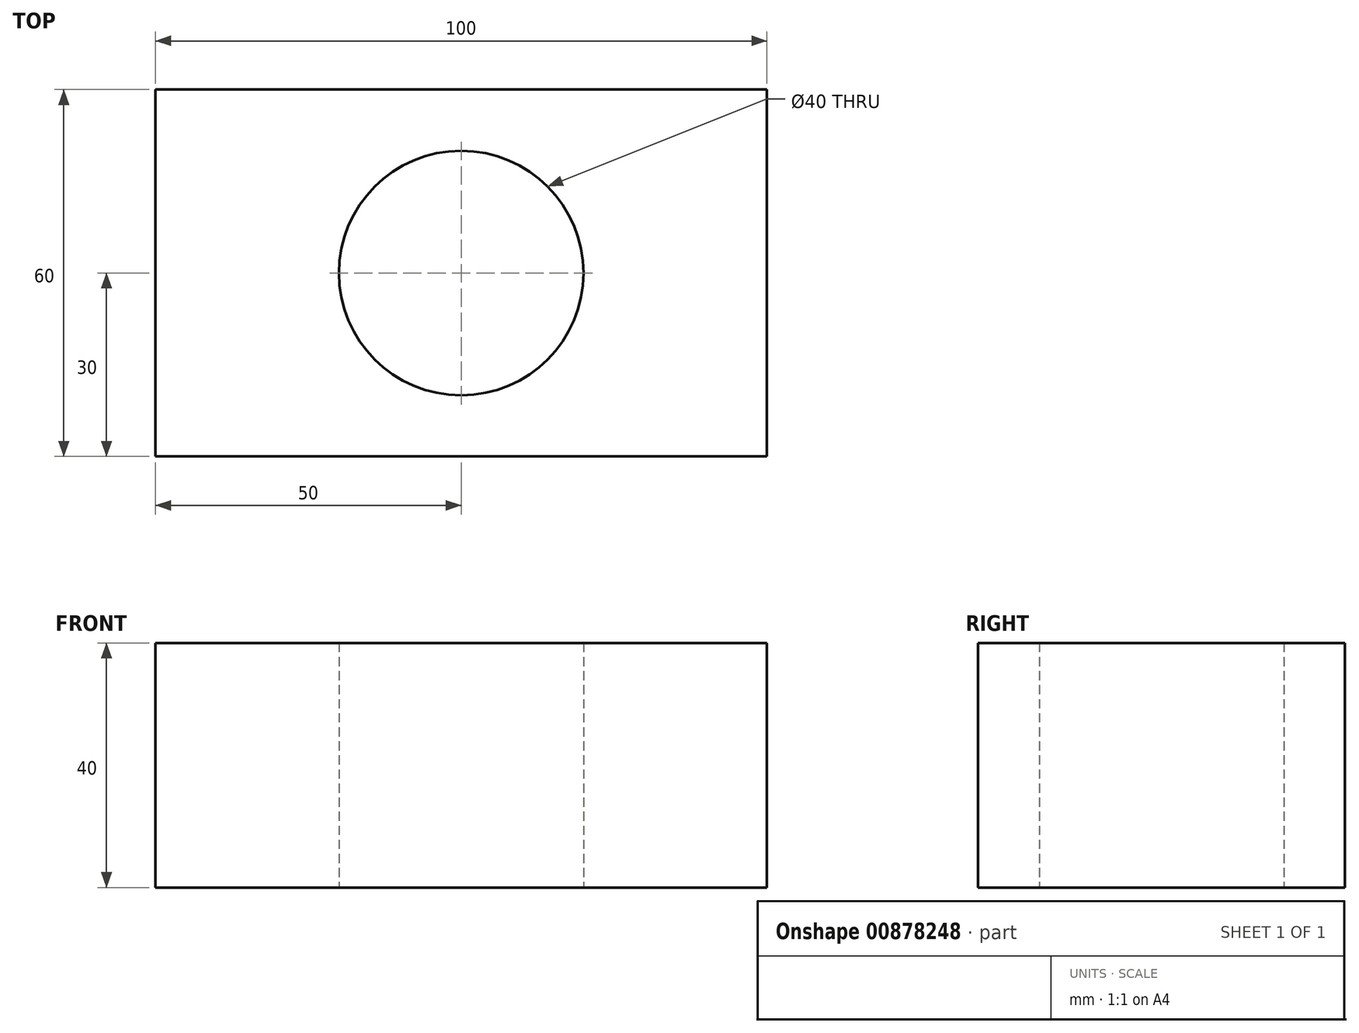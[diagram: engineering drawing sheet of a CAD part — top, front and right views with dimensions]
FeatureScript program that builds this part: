
annotation { "Feature Type Name" : "Feature", "Feature Type Description" : "" }
export const myFeature = defineFeature(function(context is Context, id is Id, definition is map)
    precondition{}
    {
        {
            var Q0;
            Q0=qCreatedBy(makeId("Top.planeOp"),FACE);
            var sketch = newSketch(context, id + "F0", { "sketchPlane" : qUnion([Q0])});
            skLineSegment(sketch, "E0.bottom", {"start": v(0, 0) * mm, "end": v(100, 0) * mm});
            skLineSegment(sketch, "E0.top", {"start": v(0, 60) * mm, "end": v(100, 60) * mm});
            skLineSegment(sketch, "E0.left", {"start": v(0, 0) * mm, "end": v(0, 60) * mm});
            skLineSegment(sketch, "E0.right", {"start": v(100, 0) * mm, "end": v(100, 60) * mm});
            skCircle(sketch, "E1", {"center": v(50, 30) * mm, "radius": 20 * mm});
            skLineSegment(sketch, "E2", {"start": v(0, 60) * mm, "end": v(100, 0) * mm, "construction": true});
            skSolve(sketch);
        }
        {
            var Q0;
            Q0=makeQuery(id+"F0.imprint","IMPRINT",FACE,{"disambiguationData":[TD([[makeQuery(id+"F0.imprint","IMPRINT",EDGE,{"derivedFrom":sQuery(id+"F0.wireOp",EDGE,"E0.bottom")}),1.0]])]});
            extrude(context, id + "F1", {"entities" : qUnion([Q0]), "depth" : 40 * mm, "offsetDistance" : 25.4 * mm});
        }
    });
